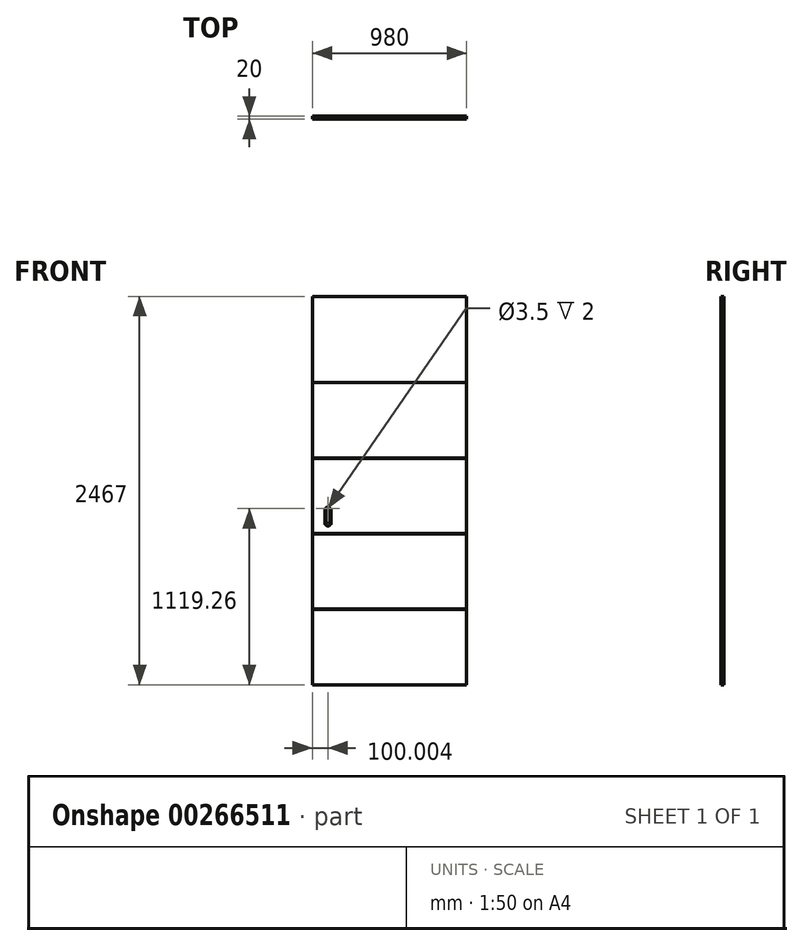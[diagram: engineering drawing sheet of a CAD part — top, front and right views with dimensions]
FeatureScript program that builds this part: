
annotation { "Feature Type Name" : "Feature", "Feature Type Description" : "" }
export const myFeature = defineFeature(function(context is Context, id is Id, definition is map)
    precondition{}
    {
        {
            var Q0;
            Q0=qCreatedBy(makeId("Front.planeOp"),FACE);
            var sketch = newSketch(context, id + "F0", { "sketchPlane" : qUnion([Q0])});
            skLineSegment(sketch, "E0.bottom", {"start": v(-661.76, 1229.1) * mm, "end": v(318.24, 1229.1) * mm});
            skLineSegment(sketch, "E0.top", {"start": v(-661.76, -1237.9) * mm, "end": v(318.24, -1237.9) * mm});
            skLineSegment(sketch, "E0.left", {"start": v(-661.76, 1229.1) * mm, "end": v(-661.76, -1237.9) * mm});
            skLineSegment(sketch, "E0.right", {"start": v(318.24, 1229.1) * mm, "end": v(318.24, -1237.9) * mm});
            skSolve(sketch);
        }
        {
            var Q0;
            Q0=makeQuery(id+"F0.imprint","IMPRINT",FACE,{"disambiguationData":[TD([[makeQuery(id+"F0.imprint","IMPRINT",EDGE,{"derivedFrom":sQuery(id+"F0.wireOp",EDGE,"E0.bottom")}),-1.0]])]});
            extrude(context, id + "F1", {"entities" : qUnion([Q0]), "depth" : 18 * mm});
        }
        {
            var Q0;
            Q0=makeQuery(id+"F1.opExtrude","SWEPT_FACE",FACE,{"disambiguationData":[OSD([sQuery(id+"F0.wireOp",EDGE,"E0.left")])]});
            var sketch = newSketch(context, id + "F2", { "sketchPlane" : qUnion([Q0])});
            skLineSegment(sketch, "E1", {"start": v(-467.06, -757.9) * mm, "end": v(625.08, -757.9) * mm, "construction": true});
            skLineSegment(sketch, "E2", {"start": v(625.08, -277.9) * mm, "end": v(-589.97, -277.9) * mm, "construction": true});
            skLineSegment(sketch, "E3", {"start": v(-589.97, 202.1) * mm, "end": v(575.92, 202.1) * mm, "construction": true});
            skLineSegment(sketch, "E4", {"start": v(575.92, 682.1) * mm, "end": v(-586.45, 682.1) * mm, "construction": true});
            skLineSegment(sketch, "E5", {"start": v(-586.45, 1229.1) * mm, "end": v(554.85, 1229.1) * mm, "construction": true});
            skLineSegment(sketch, "E6", {"start": v(0, -1237.9) * mm, "end": v(-639.13, -1237.9) * mm, "construction": true});
            skLineSegment(sketch, "E7", {"start": v(18, -756.9) * mm, "end": v(17, -757.9) * mm});
            skLineSegment(sketch, "E8", {"start": v(18, -756.9) * mm, "end": v(18, -757.9) * mm});
            skLineSegment(sketch, "E9.MirrorCS", {"start": v(18, -758.9) * mm, "end": v(17, -757.9) * mm});
            skLineSegment(sketch, "E10.MirrorCS", {"start": v(18, -758.9) * mm, "end": v(18, -757.9) * mm});
            skLineSegment(sketch, "E11", {"start": v(384.77, -277.9) * mm, "end": v(384.77, -757.9) * mm, "construction": true});
            skLineSegment(sketch, "E12", {"start": v(384.77, -517.9) * mm, "end": v(-286.08, -517.9) * mm, "construction": true});
            skLineSegment(sketch, "E13.MirrorCS", {"start": v(18, 683.1) * mm, "end": v(18, 682.1) * mm});
            skLineSegment(sketch, "E14.MirrorCS", {"start": v(18, 683.1) * mm, "end": v(17, 682.1) * mm});
            skLineSegment(sketch, "E15.MirrorCS", {"start": v(18, 681.1) * mm, "end": v(17, 682.1) * mm});
            skLineSegment(sketch, "E16.MirrorCS", {"start": v(18, 681.1) * mm, "end": v(18, 682.1) * mm});
            skLineSegment(sketch, "E17.MirrorCS", {"start": v(18, 201.1) * mm, "end": v(18, 202.1) * mm});
            skLineSegment(sketch, "E18.MirrorCS", {"start": v(18, 201.1) * mm, "end": v(17, 202.1) * mm});
            skLineSegment(sketch, "E19.MirrorCS", {"start": v(18, 203.1) * mm, "end": v(17, 202.1) * mm});
            skLineSegment(sketch, "E20.MirrorCS", {"start": v(18, 203.1) * mm, "end": v(18, 202.1) * mm});
            skLineSegment(sketch, "E21.MirrorCS", {"start": v(18, -278.9) * mm, "end": v(18, -277.9) * mm});
            skLineSegment(sketch, "E22.MirrorCS", {"start": v(18, -276.9) * mm, "end": v(17, -277.9) * mm});
            skLineSegment(sketch, "E23.MirrorCS", {"start": v(18, -278.9) * mm, "end": v(17, -277.9) * mm});
            skLineSegment(sketch, "E24.MirrorCS", {"start": v(18, -276.9) * mm, "end": v(18, -277.9) * mm});
            skSolve(sketch);
        }
        {
            var Q0;
            Q0 = qSketchRegion(id + "F2", true);
            extrude(context, id + "F3", {"entities" : qUnion([Q0]), "operationType" : NewBodyOperationType.REMOVE, "endBound" : BoundingType.THROUGH_ALL, "oppositeDirection" : true, "depth" : 25 * mm});
        }
        {
            var Q0;
            {var subQ0=sQuery(id+"F0.wireOp",EDGE,"E0.left");var subQ1=sQuery(id+"F0.wireOp",EDGE,"E0.right");Q0=makeQuery(id+"F3.boolean.opBoolean","SPLIT",FACE,{"disambiguationData":[TD([makeQuery(id+"F3.opExtrude","SWEPT_FACE",FACE,{"disambiguationData":[OSD([sQuery(id+"F2.wireOp",EDGE,"E18.MirrorCS")])]})])],"derivedFrom":makeQuery(id+"F1.opExtrude","CAP_FACE",FACE,{"disambiguationData":[OSD([sQuery(id+"F0.wireOp",EDGE,"E0.bottom"),sQuery(id+"F0.wireOp",EDGE,"E0.top"),subQ0,subQ1])],"isStart":false})});}
            var sketch = newSketch(context, id + "F4", { "sketchPlane" : qUnion([Q0])});
            skArc(sketch, "E25", {"start": v(-547.76, -137.9) * mm, "mid": v(-561.76, -123.9) * mm, "end": v(-575.76, -137.9) * mm});
            skLineSegment(sketch, "E26", {"start": v(-575.76, -137.9) * mm, "end": v(-575.76, -199.9) * mm});
            skArc(sketch, "E27", {"start": v(-575.76, -199.9) * mm, "mid": v(-561.76, -213.9) * mm, "end": v(-547.76, -199.9) * mm});
            skLineSegment(sketch, "E28", {"start": v(-547.76, -137.9) * mm, "end": v(-547.76, -199.9) * mm});
            skArc(sketch, "E29", {"start": v(-549.76, -137.9) * mm, "mid": v(-561.76, -125.9) * mm, "end": v(-573.76, -137.9) * mm});
            skArc(sketch, "E30", {"start": v(-573.76, -199.9) * mm, "mid": v(-561.76, -211.9) * mm, "end": v(-549.76, -199.9) * mm});
            skLineSegment(sketch, "E31", {"start": v(-573.76, -137.9) * mm, "end": v(-573.76, -199.9) * mm});
            skLineSegment(sketch, "E32", {"start": v(-549.76, -137.9) * mm, "end": v(-549.76, -199.9) * mm});
            skLineSegment(sketch, "E33", {"start": v(-561.76, -105.6) * mm, "end": v(-561.76, -199.9) * mm, "construction": true});
            skPoint(sketch, "E34.orphan", {"position": v(-561.76, -168.9) * mm});
            skLineSegment(sketch, "E35", {"start": v(-581.76, -168.9) * mm, "end": v(-581.76, -128.9) * mm});
            skArc(sketch, "E36.trimOffspring", {"start": v(-561.76, -108.9) * mm, "mid": v(-575.9, -114.75) * mm, "end": v(-581.76, -128.9) * mm});
            skArc(sketch, "E37.MirrorCS", {"start": v(-561.76, -108.9) * mm, "mid": v(-547.61, -114.75) * mm, "end": v(-541.76, -128.9) * mm});
            skLineSegment(sketch, "E38.MirrorCS", {"start": v(-541.76, -168.9) * mm, "end": v(-541.76, -128.9) * mm});
            skLineSegment(sketch, "E39.MirrorCS", {"start": v(-581.76, -168.9) * mm, "end": v(-581.76, -208.9) * mm});
            skArc(sketch, "E40.MirrorCS", {"start": v(-561.76, -228.9) * mm, "mid": v(-575.9, -223.03) * mm, "end": v(-581.76, -208.9) * mm});
            skArc(sketch, "E41.MirrorCS", {"start": v(-561.76, -228.9) * mm, "mid": v(-547.61, -223.03) * mm, "end": v(-541.76, -208.9) * mm});
            skLineSegment(sketch, "E42.MirrorCS", {"start": v(-541.76, -168.9) * mm, "end": v(-541.76, -208.9) * mm});
            skCircle(sketch, "E43", {"center": v(-561.76, -118.63) * mm, "radius": 1.75 * mm});
            skCircle(sketch, "E44.MirrorC", {"center": v(-482.87, -3.3) * mm, "radius": 1.75 * mm});
            skSolve(sketch);
        }
        {
            var Q0;
            Q0=makeQuery(id+"F4.imprint","IMPRINT",FACE,{"disambiguationData":[TD([[makeQuery(id+"F4.imprint","IMPRINT",EDGE,{"derivedFrom":sQuery(id+"F4.wireOp",EDGE,"E25")}),1.0]])]});
            var Q1;
            Q1=makeQuery(id+"F4.imprint","IMPRINT",FACE,{"disambiguationData":[TD([[makeQuery(id+"F4.imprint","IMPRINT",EDGE,{"derivedFrom":sQuery(id+"F4.wireOp",EDGE,"E29")}),1.0]])]});
            extrude(context, id + "F5", {"entities" : qUnion([Q0, Q1]), "operationType" : NewBodyOperationType.REMOVE, "oppositeDirection" : true, "depth" : 13 * mm});
        }
        {
            var Q0;
            Q0=makeQuery(id+"F4.imprint","IMPRINT",FACE,{"disambiguationData":[TD([[makeQuery(id+"F4.imprint","IMPRINT",EDGE,{"derivedFrom":sQuery(id+"F4.wireOp",EDGE,"E25")}),1.0]])]});
            extrude(context, id + "F6", {"entities" : qUnion([Q0]), "oppositeDirection" : true, "depth" : 13 * mm});
        }
        {
            var Q0;
            Q0=makeQuery(id+"F4.imprint","IMPRINT",FACE,{"disambiguationData":[TD([[makeQuery(id+"F4.imprint","IMPRINT",EDGE,{"derivedFrom":sQuery(id+"F4.wireOp",EDGE,"E25")}),1.0]])]});
            var Q1;
            Q1=makeQuery(id+"F4.imprint","IMPRINT",FACE,{"disambiguationData":[TD([[makeQuery(id+"F4.imprint","IMPRINT",EDGE,{"derivedFrom":sQuery(id+"F4.wireOp",EDGE,"E29")}),1.0]])]});
            extrude(context, id + "F7", {"entities" : qUnion([Q0, Q1]), "operationType" : NewBodyOperationType.ADD, "oppositeDirection" : true, "depth" : 13 * mm, "hasSecondDirection" : true, "secondDirectionOppositeDirection" : true, "secondDirectionDepth" : 11 * mm});
        }
        {
            var Q0;
            Q0=makeQuery(id+"F4.imprint","IMPRINT",FACE,{"disambiguationData":[TD([[makeQuery(id+"F4.imprint","IMPRINT",EDGE,{"derivedFrom":sQuery(id+"F4.wireOp",EDGE,"E25")}),-1.0]])]});
            var Q1;
            Q1=makeQuery(id+"F4.imprint","IMPRINT",FACE,{"disambiguationData":[TD([[makeQuery(id+"F4.imprint","IMPRINT",EDGE,{"derivedFrom":sQuery(id+"F4.wireOp",EDGE,"E25")}),1.0]])]});
            extrude(context, id + "F8", {"entities" : qUnion([Q0, Q1]), "operationType" : NewBodyOperationType.ADD, "depth" : 2 * mm});
        }
    });
